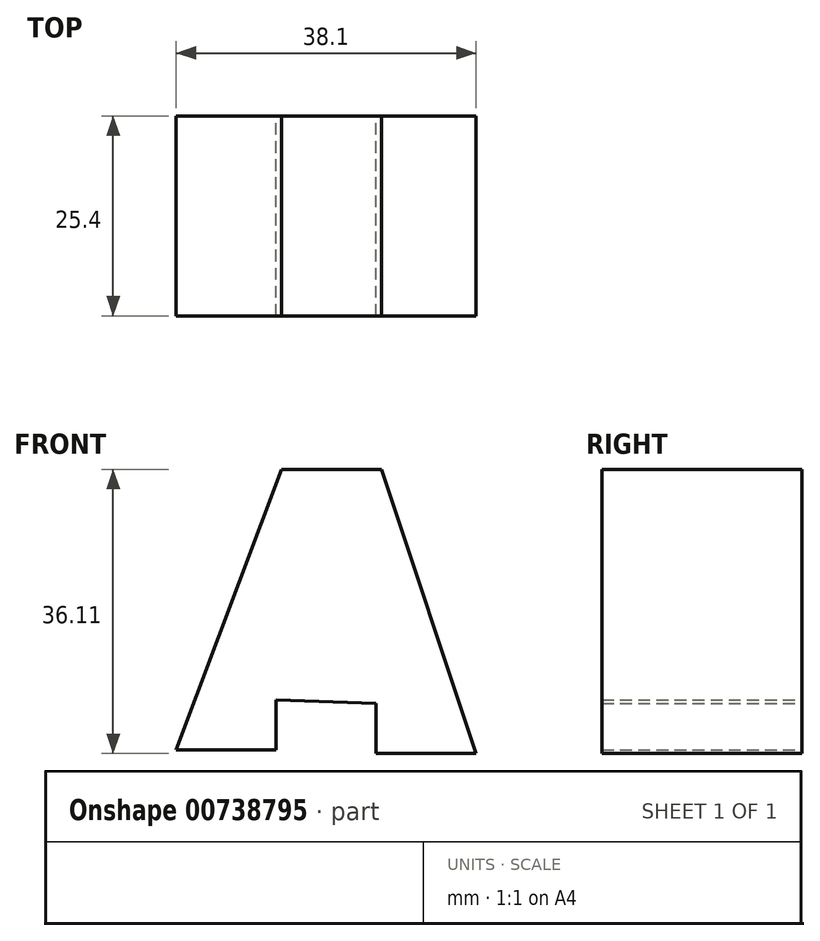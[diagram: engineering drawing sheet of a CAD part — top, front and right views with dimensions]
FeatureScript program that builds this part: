
annotation { "Feature Type Name" : "Feature", "Feature Type Description" : "" }
export const myFeature = defineFeature(function(context is Context, id is Id, definition is map)
    precondition{}
    {
        {
            var Q0;
            Q0=qCreatedBy(makeId("Front.planeOp"),FACE);
            var sketch = newSketch(context, id + "F0", { "sketchPlane" : qUnion([Q0])});
            skLineSegment(sketch, "E0", {"start": v(-6.36, 27.44) * mm, "end": v(6.34, 27.44) * mm});
            skLineSegment(sketch, "E1", {"start": v(6.34, 27.44) * mm, "end": v(18.38, -8.67) * mm});
            skLineSegment(sketch, "E2", {"start": v(18.38, -8.67) * mm, "end": v(5.68, -8.67) * mm});
            skLineSegment(sketch, "E3", {"start": v(5.68, -8.67) * mm, "end": v(5.68, -2.32) * mm});
            skLineSegment(sketch, "E4", {"start": v(5.68, -2.32) * mm, "end": v(-7.02, -1.85) * mm});
            skLineSegment(sketch, "E5", {"start": v(-7.02, -1.85) * mm, "end": v(-7.02, -8.2) * mm});
            skLineSegment(sketch, "E6", {"start": v(-7.02, -8.2) * mm, "end": v(-19.72, -8.2) * mm});
            skLineSegment(sketch, "E7", {"start": v(-19.72, -8.2) * mm, "end": v(-6.36, 27.44) * mm});
            skSolve(sketch);
        }
        {
            var Q0;
            Q0=makeQuery(id+"F0.imprint","IMPRINT",FACE,{"disambiguationData":[TD([[makeQuery(id+"F0.imprint","IMPRINT",EDGE,{"derivedFrom":sQuery(id+"F0.wireOp",EDGE,"E0")}),-1.0]])]});
            extrude(context, id + "F1", {"entities" : qUnion([Q0]), "depth" : 25.4 * mm, "offsetDistance" : 25.4 * mm});
        }
    });
